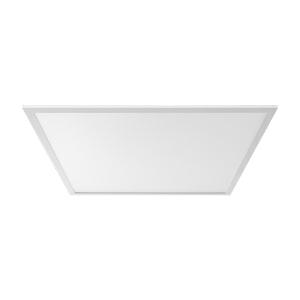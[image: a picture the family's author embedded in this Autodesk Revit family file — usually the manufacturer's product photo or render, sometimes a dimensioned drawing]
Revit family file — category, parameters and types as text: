
# Revit family: 3f_filippi_-_3f_led_panel_3f_filippi_-_22792_a01486_-_3flp6060ugr-930__1100ma____dali_834c
name_source: partatom
category: Lighting Fixtures
units: mm (PartAtom-declared; Revit-internal decimal feet)

## family parameters
Cut with Voids When Loaded = No
Host = Face
Light Source = No
Part Type = Normal
Room Calculation Point = No
Round Connector Dimension = Use Diameter
Shared = No

## types (1)
- 3F Filippi - 3F LED Panel (1 x LED, 4084 lm, 43 W, 3000 K)
    Apparent Load = 43 VA
    Approval mark = ENEC
    CIE Flux Codes = 63 89 97 100 100
    Color Rendering = 90
    Color Temperature = 3000 K
    Control Gear = Electronic transformer
    Default Elevation = 1800 mm
    Description = ILLUMINOTECHNICAL
Luminous efficiency 100% (DLOR 100%, ULOR 0%).
Initial luminous flux of the luminaire 4084 lm.
Direct symmetric distribution.
Installation Interdistance Transv.D = 1.18 x hu - Long.D = 1.30 x hu.
Average luminance <3000 cd/m² for radial angles >65°.
Tabular UGR (CIE 117 - 4H-8H; S=0.25H; 70/50/20): RUG 18.2 - 18.4.
Beam angle: 86° - 90°.
Luminous efficacy 95 lm/W.
Lifetime (L93/B10): 30000 h. (tq+25°C)
Lifetime (L90/B10): 50000 h. (tq+25°C)
Lifetime (L80/B10): 80000 h. (tq+25°C)
Lifetime (L75/B10): 100000 h. (tq+25°C)
Sudden decreased luminous flux after 50000 hours: 0% (C0).
Photobiological safety in compliance with IEC/TR 62778: RG0 risk exempt, (IEC 62471).
In compliance with IEC/EN 62722-2-1 - IEC/EN 62717 standards.

SOURCE
2 linear LED modules 930.
Energy efficiency class (UE 2019/2020 - UE 2019/2015): D.
CIE 13.3 Colour rendering index: CRI >90 (R9 >50%).
IES TM-30 Fidelity Index: Rf = 90 Rg = 98.
CCT nominal colour temperature 3000 K.
Colour initial tolerance (MacAdam): SDCM 3.

MECHANICAL
Housing in white painted epoxy-polyester powder aluminium.
Diffuser in SMP trasparent microprismatic methacrylate (PMMA) externally, anti-glare with high transmittance.
Perimetral frame in white polycarbonate.
Anti-fall safety cable.
Luminaire with limited surface temperature. - D - (EN 60598-2-24)
Dimensions: 595x595 mm, height 9 mm. Weight 2.54 kg.
IP43 protection degree for exposed part, IP20 for recessed part.
Mechanical strength to impacts IK06 (1 joule).
Glow-wire test resistance 650°C.

ELECTRICAL
Wiring on a separate unit (Multi-current power supply, to be ordered separately).
Power of the luminaire 43 W.
CE - IEC 60598-1 - EN 60598-1.
SAFE FLICKER: PstLM=<1 and SVM=<0.4 (IEC TR 61547-1 and IEC TR 63158), to ensure a more comfortable and safe light.
Luminaire compliant with EN 60598-2-22 for power supply from a centralised emergency system CPSS (Central Power Supply System), not incorporated in the luminaire - high risk areas excluded. The default power and flux are 100% in AC and 100% in DC.
Ambient temperature from 0°C to +25°C.
Temperature class T6 max 85°C.
Relative humidity UR: <85%.

INSTALLATION
Lay-in recessed fitting / Pull-up recessed fitting with brackets / Ceiling installation with frame / Suspension via accessory.
All accessories dedicated to this product are available on the Catalog and on our website www.3F-Filippi.com.

ACCESSORIES
A01486 - DELT40C-MEL DRIVER DALI DIP-SWITCH.
DALI, PUSH-DIM, electronic wiring 230V-50/60Hz, power factor 0.95 at full load, constant output current, SELV, class II, 1 driver, 1 DALI addresse.
Multi-current power supply that allows you to choose the driving current of the fixture at the time of installation (default 900mA) according to the required illuminance.
Quick connection non-reversible plug-socket terminal block, also for cascade connection.

APPLICATIONS
Suitable product for food production plants (HACCP), IFS (Food Version 6), BRC (GSFS Food Version 7).
Environments: with VDTs, meeting rooms, offices.
Environments: recreational, transit areas, corridors, schools, stairwells.
Environments where soft diffuse light is required for optimal visual comfort.

WARNING
Luminaire designed for disposal/recycling at end-of-life.
Replaceable control gear by a professional.
    Height = 0 mm  [stored 0 ft]
    Lamp = 1 x LED
    Lamp Light Flux = 4084 lm
    Lamp Power = 43 W
    Lamp count = 1
    Length = 595 mm
    Lifetime = 50000 h
    Luminous efficacy = 95 lm/W
    Manufacturer = 3F Filippi
    ModVariant = No
    Model = 3F Filippi - 22792+A01486 - 3FLP6060UGR-930 (1100mA) + DALI
    Mounting Place = Ceiling
    Mounting Type = Recessed
    Number of Poles = 1
    OnlyDefault = Yes
    Power Factor = 1
    Product Name = 3F Filippi - 3F LED Panel
    Product group = recessed luminaire
    ProductGroupID = 4
    Protection Class = Protection class II
    Protection Degree = IP 20
    RLX_Detail_Level = 1
    RLX_Emergency_Light_Flux = 0 lm
    RLX_Emergency_Type = 0
    RLX_Emergency_Type_DB = No
    RlxData = <blob elided: 32025 chars, md5=cf7b4fd6>
    Socket = socket
    Standby Power = 0 W
    System Light Flux = 4084 lm
    System Power = 43 W
    Type Comments = Product without accessories
    Type Image = 3ffilippi_3f_led_panel_596x596.jpg
    URL = http://relux.com
    VarID = ---
    Voltage = 0 V
    Weight = 0.00 kg
    Width = 595 mm

note: [stored X ft] marks values corroborated as IEEE doubles in the binary element streams (Revit-internal decimal feet)

## geometry (parser evidence)
native form markers: Blend x4, Sweep x12
no freeform markers — native parametric forms only
